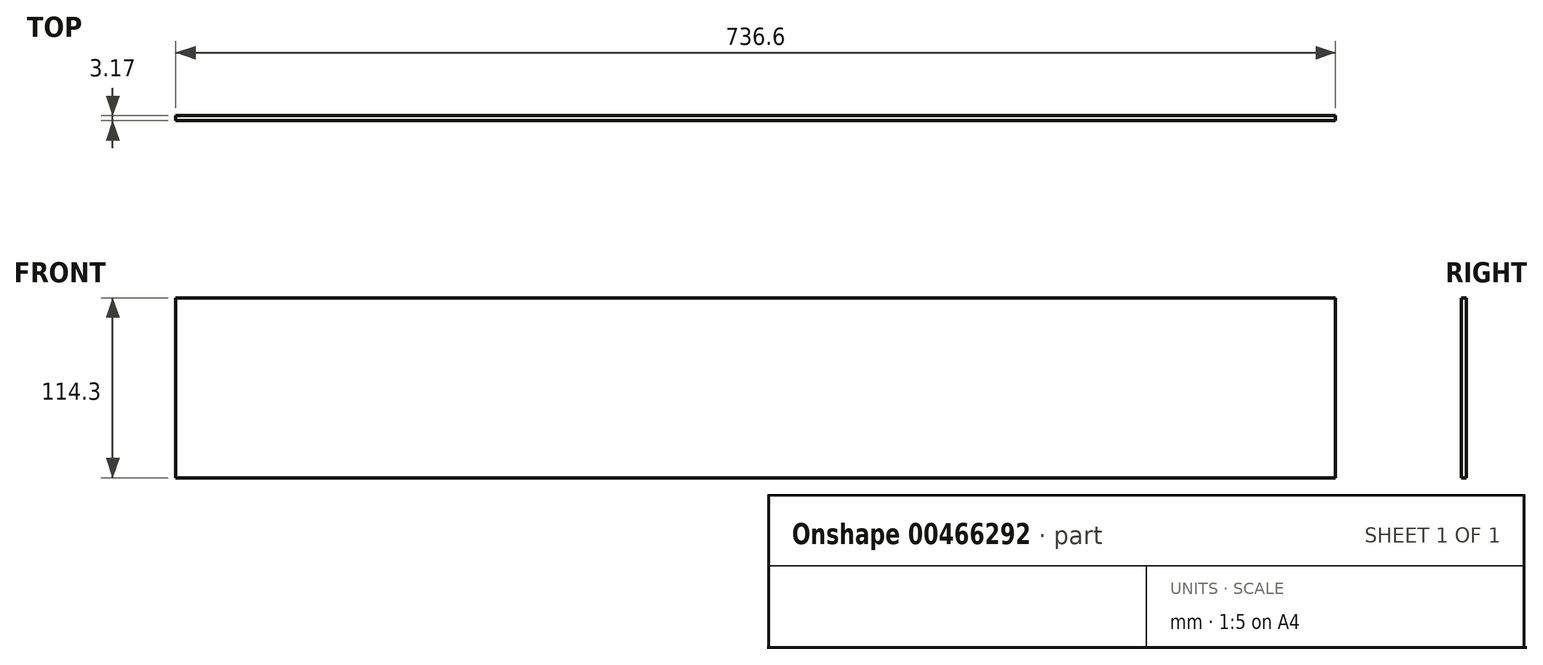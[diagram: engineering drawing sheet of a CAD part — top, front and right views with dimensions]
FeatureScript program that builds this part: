
annotation { "Feature Type Name" : "Feature", "Feature Type Description" : "" }
export const myFeature = defineFeature(function(context is Context, id is Id, definition is map)
    precondition{}
    {
        {
            var Q0;
            Q0=qCreatedBy(makeId("Front.planeOp"),FACE);
            var sketch = newSketch(context, id + "F0", { "sketchPlane" : qUnion([Q0])});
            skLineSegment(sketch, "E0", {"start": v(-470.12, 137.46) * mm, "end": v(266.48, 137.46) * mm});
            skLineSegment(sketch, "E1", {"start": v(266.48, 137.46) * mm, "end": v(266.48, 23.16) * mm});
            skLineSegment(sketch, "E2", {"start": v(266.48, 23.16) * mm, "end": v(-470.12, 23.16) * mm});
            skLineSegment(sketch, "E3", {"start": v(-470.12, 23.16) * mm, "end": v(-470.12, 137.46) * mm});
            skSolve(sketch);
        }
        {
            var Q0;
            Q0=qSketchRegion(id+"F0",true);
            extrude(context, id + "F1", {"entities" : qUnion([Q0]), "depth" : 3.17 * mm, "offsetDistance" : 25.4 * mm});
        }
    });
